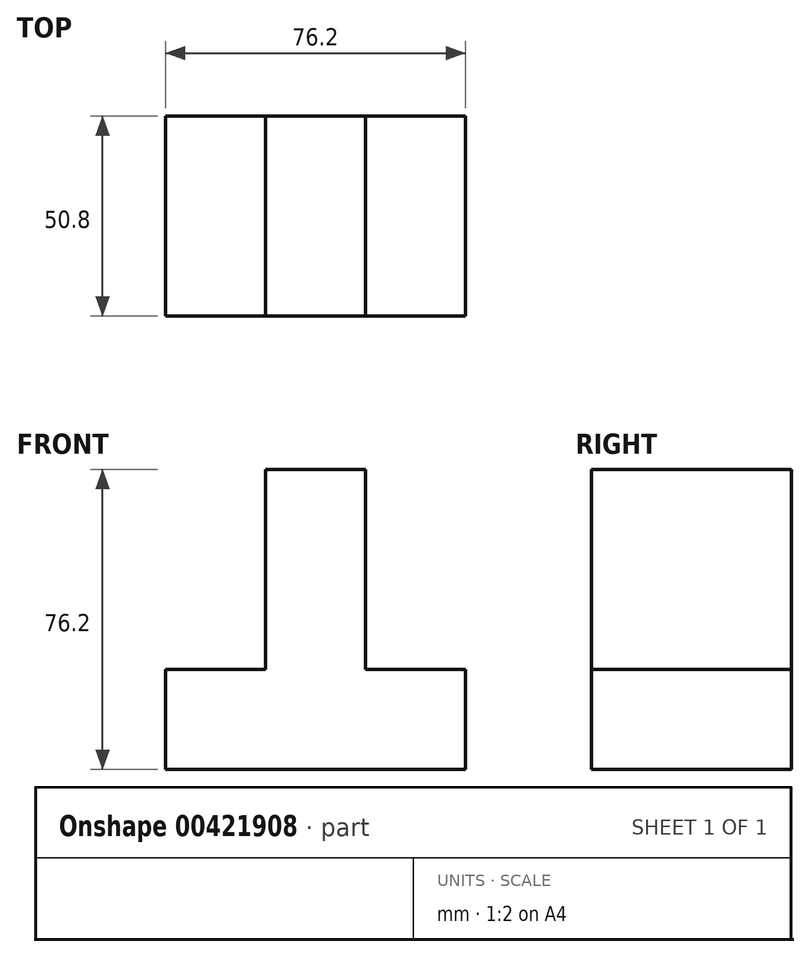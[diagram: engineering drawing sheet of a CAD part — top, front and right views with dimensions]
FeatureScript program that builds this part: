
annotation { "Feature Type Name" : "Feature", "Feature Type Description" : "" }
export const myFeature = defineFeature(function(context is Context, id is Id, definition is map)
    precondition{}
    {
        {
            var Q0;
            Q0=qCreatedBy(makeId("Front.planeOp"),FACE);
            var sketch = newSketch(context, id + "F0", { "sketchPlane" : qUnion([Q0])});
            skLineSegment(sketch, "E0", {"start": v(-50.8, 0) * mm, "end": v(25.4, 0) * mm});
            skLineSegment(sketch, "E1", {"start": v(-50.8, 0) * mm, "end": v(-50.8, 25.4) * mm});
            skLineSegment(sketch, "E2", {"start": v(25.4, 0) * mm, "end": v(25.4, 25.4) * mm});
            skLineSegment(sketch, "E3", {"start": v(-50.8, 25.4) * mm, "end": v(-25.4, 25.4) * mm});
            skLineSegment(sketch, "E4", {"start": v(25.4, 25.4) * mm, "end": v(0, 25.4) * mm});
            skLineSegment(sketch, "E5", {"start": v(0, 25.4) * mm, "end": v(0, 76.2) * mm});
            skLineSegment(sketch, "E6", {"start": v(-25.4, 25.4) * mm, "end": v(-25.4, 76.2) * mm});
            skLineSegment(sketch, "E7", {"start": v(-25.4, 76.2) * mm, "end": v(0, 76.2) * mm});
            skSolve(sketch);
        }
        {
            var Q0;
            Q0=makeQuery(id+"F0.imprint","IMPRINT",FACE,{"disambiguationData":[TD([[makeQuery(id+"F0.imprint","IMPRINT",EDGE,{"derivedFrom":sQuery(id+"F0.wireOp",EDGE,"E0")}),1.0]])]});
            extrude(context, id + "F1", {"entities" : qUnion([Q0]), "depth" : 50.8 * mm});
        }
    });
